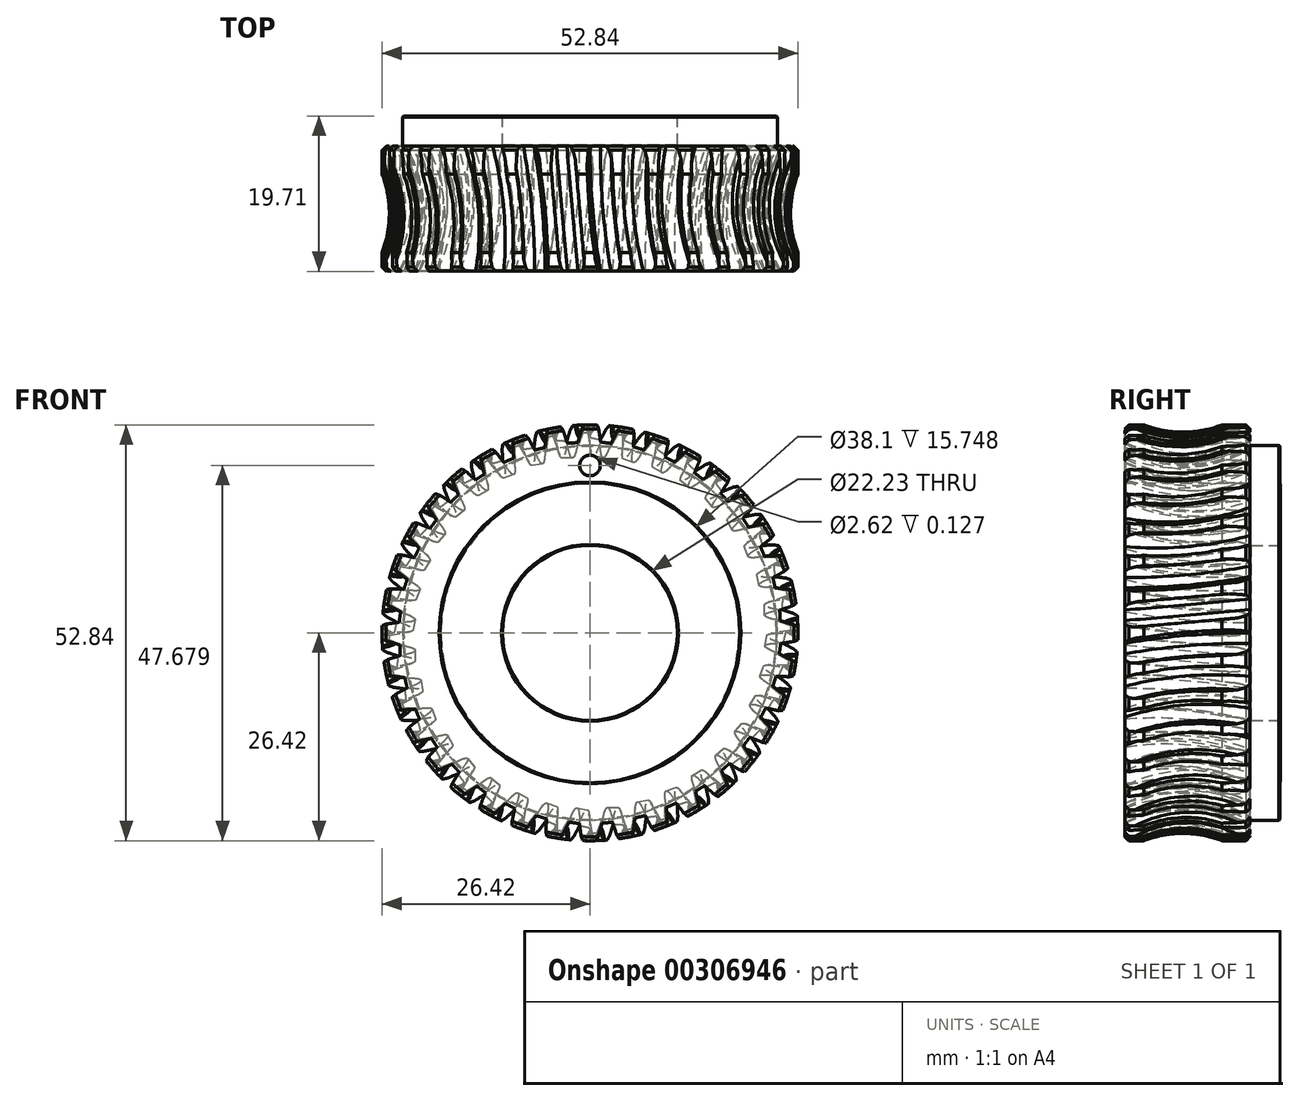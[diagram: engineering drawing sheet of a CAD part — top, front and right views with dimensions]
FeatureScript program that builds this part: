
annotation { "Feature Type Name" : "Feature", "Feature Type Description" : "" }
export const myFeature = defineFeature(function(context is Context, id is Id, definition is map)
    precondition{}
    {
        {
            var Q0;
            Q0=qCreatedBy(makeId("Front.planeOp"),FACE);
            var sketch = newSketch(context, id + "F0", { "sketchPlane" : qUnion([Q0])});
            skCircle(sketch, "E0", {"center": v(0, 0) * mm, "radius": 26.42 * mm});
            skCircle(sketch, "E1", {"center": v(0, 0) * mm, "radius": 11.11 * mm});
            skCircle(sketch, "E2", {"center": v(0, 0) * mm, "radius": 19.05 * mm});
            skSolve(sketch);
        }
        {
            var Q0;
            Q0=makeQuery(id+"F0.imprint","IMPRINT",FACE,{"disambiguationData":[TD([[makeQuery(id+"F0.imprint","IMPRINT",EDGE,{"derivedFrom":sQuery(id+"F0.wireOp",EDGE,"E0")}),1.0]])]});
            extrude(context, id + "F1", {"entities" : qUnion([Q0]), "endBound" : BoundingType.SYMMETRIC, "depth" : 15.88 * mm});
        }
        {
            var Q0;
            Q0=makeQuery(id+"F1.opExtrude","CAP_EDGE",EDGE,{"disambiguationData":[OSD([sQuery(id+"F0.wireOp",EDGE,"E0")])],"isStart":true});
            var Q1;
            Q1=makeQuery(id+"F1.opExtrude","CAP_EDGE",EDGE,{"disambiguationData":[OSD([sQuery(id+"F0.wireOp",EDGE,"E0")])],"isStart":false});
            chamfer(context, id + "F2", {"entities" : qUnion([Q0, Q1]), "width" : 0.5 * mm, "tangentPropagation" : true});
        }
        {
            var Q0;
            Q0=qCreatedBy(makeId("Top.planeOp"),FACE);
            var sketch = newSketch(context, id + "F3", { "sketchPlane" : qUnion([Q0])});
            skLineSegment(sketch, "E3", {"start": v(-49.13, -51.5) * mm, "end": v(57.98, -51.5) * mm});
            skSolve(sketch);
        }
        {
            var Q0;
            Q0=sQuery(id+"F3.wireOp",EDGE,"E3");
            cPlane(context, id + "F4", {"entities" : qUnion([Q0]), "cplaneType" : CPlaneType.LINE_ANGLE, "offset" : 25.4 * mm, "angle" : 85 * degree, "oppositeDirection" : true, "width" : 152.4 * mm, "height" : 152.4 * mm});
        }
        {
            var Q0;
            Q0=qCreatedBy(id+"F4.planeOp",FACE);
            var sketch = newSketch(context, id + "F5", { "sketchPlane" : qUnion([Q0])});
            skCircle(sketch, "E4", {"center": v(38.56, 0) * mm, "radius": 16.37 * mm});
            skCircle(sketch, "E5", {"center": v(38.56, 0) * mm, "radius": 13.48 * mm});
            skSolve(sketch);
        }
        {
            var Q0;
            Q0=makeQuery(id+"F5.imprint","IMPRINT",FACE,{"disambiguationData":[TD([[makeQuery(id+"F5.imprint","IMPRINT",EDGE,{"derivedFrom":sQuery(id+"F5.wireOp",EDGE,"E4")}),1.0]])]});
            var Q1;
            Q1=makeQuery(id+"F5.imprint","IMPRINT",FACE,{"disambiguationData":[TD([[makeQuery(id+"F5.imprint","IMPRINT",EDGE,{"derivedFrom":sQuery(id+"F5.wireOp",EDGE,"E5")}),1.0]])]});
            extrude(context, id + "F6", {"entities" : qUnion([Q0, Q1]), "depth" : 3.17 * mm});
        }
        {
            var Q0;
            Q0=makeQuery(id+"F6.opExtrude","CAP_EDGE",EDGE,{"disambiguationData":[OSD([sQuery(id+"F5.wireOp",EDGE,"E4")])],"isStart":false});
            var Q1;
            Q1=makeQuery(id+"F6.opExtrude","CAP_EDGE",EDGE,{"disambiguationData":[OSD([sQuery(id+"F5.wireOp",EDGE,"E4")])],"isStart":true});
            chamfer(context, id + "F7", {"entities" : qUnion([Q0, Q1]), "chamferType" : ChamferType.OFFSET_ANGLE, "width" : 2.54 * mm, "oppositeDirection" : false, "angle" : 20 * degree, "tangentPropagation" : true});
        }
        {
            var Q0;
            Q0=makeQuery(id+"F6.opExtrude","SWEPT_BODY",BODY,{"disambiguationData":[OSD([sQuery(id+"F5.wireOp",EDGE,"E4")])]});
            var Q1;
            Q1=makeQuery(id+"F1.opExtrude","SWEPT_FACE",FACE,{"disambiguationData":[OSD([sQuery(id+"F0.wireOp",EDGE,"E2")])]});
            circularPattern(context, id + "F8", {"entities" : qUnion([Q0]), "axis" : qUnion([Q1]), "angle" : 360 * degree, "instanceCount" : 36, "equalSpace" : true});
        }
        {
            var Q0;
            Q0=makeQuery(id+"F8.opPattern","COPY",BODY,{"derivedFrom":makeQuery(id+"F6.opExtrude","SWEPT_BODY",BODY,{"disambiguationData":[OSD([sQuery(id+"F5.wireOp",EDGE,"E4")])]}),"instanceName":"25"});
            var Q1;
            Q1=makeQuery(id+"F8.opPattern","COPY",BODY,{"derivedFrom":makeQuery(id+"F6.opExtrude","SWEPT_BODY",BODY,{"disambiguationData":[OSD([sQuery(id+"F5.wireOp",EDGE,"E4")])]}),"instanceName":"24"});
            var Q2;
            Q2=makeQuery(id+"F8.opPattern","COPY",BODY,{"derivedFrom":makeQuery(id+"F6.opExtrude","SWEPT_BODY",BODY,{"disambiguationData":[OSD([sQuery(id+"F5.wireOp",EDGE,"E4")])]}),"instanceName":"23"});
            var Q3;
            Q3=makeQuery(id+"F8.opPattern","COPY",BODY,{"derivedFrom":makeQuery(id+"F6.opExtrude","SWEPT_BODY",BODY,{"disambiguationData":[OSD([sQuery(id+"F5.wireOp",EDGE,"E4")])]}),"instanceName":"22"});
            var Q4;
            Q4=makeQuery(id+"F8.opPattern","COPY",BODY,{"derivedFrom":makeQuery(id+"F6.opExtrude","SWEPT_BODY",BODY,{"disambiguationData":[OSD([sQuery(id+"F5.wireOp",EDGE,"E4")])]}),"instanceName":"21"});
            var Q5;
            Q5=makeQuery(id+"F8.opPattern","COPY",BODY,{"derivedFrom":makeQuery(id+"F6.opExtrude","SWEPT_BODY",BODY,{"disambiguationData":[OSD([sQuery(id+"F5.wireOp",EDGE,"E4")])]}),"instanceName":"20"});
            var Q6;
            Q6=makeQuery(id+"F8.opPattern","COPY",BODY,{"derivedFrom":makeQuery(id+"F6.opExtrude","SWEPT_BODY",BODY,{"disambiguationData":[OSD([sQuery(id+"F5.wireOp",EDGE,"E4")])]}),"instanceName":"19"});
            var Q7;
            Q7=makeQuery(id+"F8.opPattern","COPY",BODY,{"derivedFrom":makeQuery(id+"F6.opExtrude","SWEPT_BODY",BODY,{"disambiguationData":[OSD([sQuery(id+"F5.wireOp",EDGE,"E4")])]}),"instanceName":"18"});
            var Q8;
            Q8=makeQuery(id+"F8.opPattern","COPY",BODY,{"derivedFrom":makeQuery(id+"F6.opExtrude","SWEPT_BODY",BODY,{"disambiguationData":[OSD([sQuery(id+"F5.wireOp",EDGE,"E4")])]}),"instanceName":"17"});
            var Q9;
            Q9=makeQuery(id+"F8.opPattern","COPY",BODY,{"derivedFrom":makeQuery(id+"F6.opExtrude","SWEPT_BODY",BODY,{"disambiguationData":[OSD([sQuery(id+"F5.wireOp",EDGE,"E4")])]}),"instanceName":"16"});
            var Q10;
            Q10=makeQuery(id+"F8.opPattern","COPY",BODY,{"derivedFrom":makeQuery(id+"F6.opExtrude","SWEPT_BODY",BODY,{"disambiguationData":[OSD([sQuery(id+"F5.wireOp",EDGE,"E4")])]}),"instanceName":"15"});
            var Q11;
            Q11=makeQuery(id+"F8.opPattern","COPY",BODY,{"derivedFrom":makeQuery(id+"F6.opExtrude","SWEPT_BODY",BODY,{"disambiguationData":[OSD([sQuery(id+"F5.wireOp",EDGE,"E4")])]}),"instanceName":"14"});
            var Q12;
            Q12=makeQuery(id+"F8.opPattern","COPY",BODY,{"derivedFrom":makeQuery(id+"F6.opExtrude","SWEPT_BODY",BODY,{"disambiguationData":[OSD([sQuery(id+"F5.wireOp",EDGE,"E4")])]}),"instanceName":"13"});
            var Q13;
            Q13=makeQuery(id+"F8.opPattern","COPY",BODY,{"derivedFrom":makeQuery(id+"F6.opExtrude","SWEPT_BODY",BODY,{"disambiguationData":[OSD([sQuery(id+"F5.wireOp",EDGE,"E4")])]}),"instanceName":"12"});
            var Q14;
            Q14=makeQuery(id+"F8.opPattern","COPY",BODY,{"derivedFrom":makeQuery(id+"F6.opExtrude","SWEPT_BODY",BODY,{"disambiguationData":[OSD([sQuery(id+"F5.wireOp",EDGE,"E4")])]}),"instanceName":"11"});
            var Q15;
            Q15=makeQuery(id+"F8.opPattern","COPY",BODY,{"derivedFrom":makeQuery(id+"F6.opExtrude","SWEPT_BODY",BODY,{"disambiguationData":[OSD([sQuery(id+"F5.wireOp",EDGE,"E4")])]}),"instanceName":"10"});
            var Q16;
            Q16=makeQuery(id+"F8.opPattern","COPY",BODY,{"derivedFrom":makeQuery(id+"F6.opExtrude","SWEPT_BODY",BODY,{"disambiguationData":[OSD([sQuery(id+"F5.wireOp",EDGE,"E4")])]}),"instanceName":"9"});
            var Q17;
            Q17=makeQuery(id+"F8.opPattern","COPY",BODY,{"derivedFrom":makeQuery(id+"F6.opExtrude","SWEPT_BODY",BODY,{"disambiguationData":[OSD([sQuery(id+"F5.wireOp",EDGE,"E4")])]}),"instanceName":"8"});
            var Q18;
            Q18=makeQuery(id+"F8.opPattern","COPY",BODY,{"derivedFrom":makeQuery(id+"F6.opExtrude","SWEPT_BODY",BODY,{"disambiguationData":[OSD([sQuery(id+"F5.wireOp",EDGE,"E4")])]}),"instanceName":"7"});
            var Q19;
            Q19=makeQuery(id+"F8.opPattern","COPY",BODY,{"derivedFrom":makeQuery(id+"F6.opExtrude","SWEPT_BODY",BODY,{"disambiguationData":[OSD([sQuery(id+"F5.wireOp",EDGE,"E4")])]}),"instanceName":"6"});
            var Q20;
            Q20=makeQuery(id+"F8.opPattern","COPY",BODY,{"derivedFrom":makeQuery(id+"F6.opExtrude","SWEPT_BODY",BODY,{"disambiguationData":[OSD([sQuery(id+"F5.wireOp",EDGE,"E4")])]}),"instanceName":"5"});
            var Q21;
            Q21=makeQuery(id+"F8.opPattern","COPY",BODY,{"derivedFrom":makeQuery(id+"F6.opExtrude","SWEPT_BODY",BODY,{"disambiguationData":[OSD([sQuery(id+"F5.wireOp",EDGE,"E4")])]}),"instanceName":"4"});
            var Q22;
            Q22=makeQuery(id+"F8.opPattern","COPY",BODY,{"derivedFrom":makeQuery(id+"F6.opExtrude","SWEPT_BODY",BODY,{"disambiguationData":[OSD([sQuery(id+"F5.wireOp",EDGE,"E4")])]}),"instanceName":"3"});
            var Q23;
            Q23=makeQuery(id+"F8.opPattern","COPY",BODY,{"derivedFrom":makeQuery(id+"F6.opExtrude","SWEPT_BODY",BODY,{"disambiguationData":[OSD([sQuery(id+"F5.wireOp",EDGE,"E4")])]}),"instanceName":"2"});
            var Q24;
            Q24=makeQuery(id+"F8.opPattern","COPY",BODY,{"derivedFrom":makeQuery(id+"F6.opExtrude","SWEPT_BODY",BODY,{"disambiguationData":[OSD([sQuery(id+"F5.wireOp",EDGE,"E4")])]}),"instanceName":"1"});
            var Q25;
            Q25=makeQuery(id+"F6.opExtrude","SWEPT_BODY",BODY,{"disambiguationData":[OSD([sQuery(id+"F5.wireOp",EDGE,"E4")])]});
            var Q26;
            Q26=makeQuery(id+"F8.opPattern","COPY",BODY,{"derivedFrom":makeQuery(id+"F6.opExtrude","SWEPT_BODY",BODY,{"disambiguationData":[OSD([sQuery(id+"F5.wireOp",EDGE,"E4")])]}),"instanceName":"35"});
            var Q27;
            Q27=makeQuery(id+"F8.opPattern","COPY",BODY,{"derivedFrom":makeQuery(id+"F6.opExtrude","SWEPT_BODY",BODY,{"disambiguationData":[OSD([sQuery(id+"F5.wireOp",EDGE,"E4")])]}),"instanceName":"34"});
            var Q28;
            Q28=makeQuery(id+"F8.opPattern","COPY",BODY,{"derivedFrom":makeQuery(id+"F6.opExtrude","SWEPT_BODY",BODY,{"disambiguationData":[OSD([sQuery(id+"F5.wireOp",EDGE,"E4")])]}),"instanceName":"33"});
            var Q29;
            Q29=makeQuery(id+"F8.opPattern","COPY",BODY,{"derivedFrom":makeQuery(id+"F6.opExtrude","SWEPT_BODY",BODY,{"disambiguationData":[OSD([sQuery(id+"F5.wireOp",EDGE,"E4")])]}),"instanceName":"32"});
            var Q30;
            Q30=makeQuery(id+"F8.opPattern","COPY",BODY,{"derivedFrom":makeQuery(id+"F6.opExtrude","SWEPT_BODY",BODY,{"disambiguationData":[OSD([sQuery(id+"F5.wireOp",EDGE,"E4")])]}),"instanceName":"31"});
            var Q31;
            Q31=makeQuery(id+"F8.opPattern","COPY",BODY,{"derivedFrom":makeQuery(id+"F6.opExtrude","SWEPT_BODY",BODY,{"disambiguationData":[OSD([sQuery(id+"F5.wireOp",EDGE,"E4")])]}),"instanceName":"30"});
            var Q32;
            Q32=makeQuery(id+"F8.opPattern","COPY",BODY,{"derivedFrom":makeQuery(id+"F6.opExtrude","SWEPT_BODY",BODY,{"disambiguationData":[OSD([sQuery(id+"F5.wireOp",EDGE,"E4")])]}),"instanceName":"29"});
            var Q33;
            Q33=makeQuery(id+"F8.opPattern","COPY",BODY,{"derivedFrom":makeQuery(id+"F6.opExtrude","SWEPT_BODY",BODY,{"disambiguationData":[OSD([sQuery(id+"F5.wireOp",EDGE,"E4")])]}),"instanceName":"28"});
            var Q34;
            Q34=makeQuery(id+"F8.opPattern","COPY",BODY,{"derivedFrom":makeQuery(id+"F6.opExtrude","SWEPT_BODY",BODY,{"disambiguationData":[OSD([sQuery(id+"F5.wireOp",EDGE,"E4")])]}),"instanceName":"27"});
            var Q35;
            Q35=makeQuery(id+"F8.opPattern","COPY",BODY,{"derivedFrom":makeQuery(id+"F6.opExtrude","SWEPT_BODY",BODY,{"disambiguationData":[OSD([sQuery(id+"F5.wireOp",EDGE,"E4")])]}),"instanceName":"26"});
            var Q36;
            Q36=makeQuery(id+"F1.opExtrude","SWEPT_BODY",BODY,{"disambiguationData":[OSD([sQuery(id+"F0.wireOp",EDGE,"E0"),sQuery(id+"F0.wireOp",EDGE,"E2")])]});
            booleanBodies(context, id + "F9", {"operationType" : BooleanOperationType.SUBTRACTION, "tools" : qUnion([Q0, Q1, Q2, Q3, Q4, Q5, Q6, Q7, Q8, Q9, Q10, Q11, Q12, Q13, Q14, Q15, Q16, Q17, Q18, Q19, Q20, Q21, Q22, Q23, Q24, Q25, Q26, Q27, Q28, Q29, Q30, Q31, Q32, Q33, Q34, Q35]), "targets" : qUnion([Q36])});
        }
        {
            var Q0;
            Q0=makeQuery(id+"F5.imprint","IMPRINT",FACE,{"disambiguationData":[TD([[makeQuery(id+"F5.imprint","IMPRINT",EDGE,{"derivedFrom":sQuery(id+"F5.wireOp",EDGE,"E5")}),1.0]])]});
            var Q1;
            Q1=makeQuery(id+"F1.opExtrude","SWEPT_FACE",FACE,{"disambiguationData":[OSD([sQuery(id+"F0.wireOp",EDGE,"E2")])]});
            revolve(context, id + "F10", {"operationType" : NewBodyOperationType.REMOVE, "entities" : qUnion([Q0]), "axis" : qUnion([Q1]), "revolveType" : RevolveType.FULL, "oppositeDirection" : true});
        }
        {
            var Q0;
            Q0=makeQuery(id+"F1.opExtrude","CAP_FACE",FACE,{"disambiguationData":[OSD([sQuery(id+"F0.wireOp",EDGE,"E0"),sQuery(id+"F0.wireOp",EDGE,"E2")])],"isStart":true});
            var sketch = newSketch(context, id + "F11", { "sketchPlane" : qUnion([Q0])});
            skCircle(sketch, "E6", {"center": v(0, 0) * mm, "radius": 23.81 * mm});
            skSolve(sketch);
        }
        {
            var Q0;
            {var subQ2=sQuery(id+"F0.wireOp",EDGE,"E2");Q0=makeQuery(id+"F11.imprint","IMPRINT",FACE,{"disambiguationData":[TD([[makeQuery(id+"F11.imprint","IMPRINT",EDGE,{"derivedFrom":makeQuery(id+"F1.opExtrude","CAP_EDGE",EDGE,{"disambiguationData":[OSD([subQ2])],"isStart":true})}),1.0]])]});}
            extrude(context, id + "F12", {"entities" : qUnion([Q0]), "operationType" : NewBodyOperationType.ADD, "depth" : 3.8 * mm});
        }
        {
            var Q0;
            Q0=makeQuery(id+"F12.opExtrude","CAP_FACE",FACE,{"disambiguationData":[OSD([sQuery(id+"F0.wireOp",EDGE,"E0"),sQuery(id+"F0.wireOp",EDGE,"E2"),sQuery(id+"FC3Jd3sHyPeDAeg_1.wireOp",EDGE,"79b9966f-34db-4600-b145-85a5b1c19bfb"),sQuery(id+"F11.wireOp",EDGE,"E6")])],"isStart":false});
            var sketch = newSketch(context, id + "F13", { "sketchPlane" : qUnion([Q0])});
            skCircle(sketch, "E7", {"center": v(0, 0) * mm, "radius": 19.05 * mm});
            skSolve(sketch);
        }
        {
            var Q0;
            Q0=makeQuery(id+"F13.imprint","IMPRINT",FACE,{"disambiguationData":[TD([[makeQuery(id+"F13.imprint","IMPRINT",EDGE,{"derivedFrom":sQuery(id+"F13.wireOp",EDGE,"E7")}),-1.0]])]});
            extrude(context, id + "F14", {"entities" : qUnion([Q0]), "operationType" : NewBodyOperationType.ADD, "depth" : 9 / 406.4 * mm, "hasSecondDirection" : true, "secondDirectionOppositeDirection" : true, "secondDirectionDepth" : 3.8 * mm});
        }
        {
            var Q0;
            Q0=makeQuery(id+"F14.opExtrude","CAP_FACE",FACE,{"disambiguationData":[OSD([sQuery(id+"F13.wireOp",EDGE,"E7")])],"isStart":false});
            var sketch = newSketch(context, id + "F15", { "sketchPlane" : qUnion([Q0])});
            skCircle(sketch, "E8", {"center": v(0, 0) * mm, "radius": 11.11 * mm});
            skSolve(sketch);
        }
        {
            var Q0;
            Q0=makeQuery(id+"F15.imprint","IMPRINT",FACE,{"disambiguationData":[TD([[makeQuery(id+"F15.imprint","IMPRINT",EDGE,{"derivedFrom":sQuery(id+"F15.wireOp",EDGE,"E8")}),1.0]])]});
            extrude(context, id + "F16", {"entities" : qUnion([Q0]), "operationType" : NewBodyOperationType.REMOVE, "endBound" : BoundingType.THROUGH_ALL, "oppositeDirection" : true, "depth" : 25.4 * mm});
        }
        {
            var Q0;
            Q0=qCreatedBy(makeId("Right.planeOp"),FACE);
            var sketch = newSketch(context, id + "F17", { "sketchPlane" : qUnion([Q0])});
            skLineSegment(sketch, "E9.bottom", {"start": v(15.58, 19.07) * mm, "end": v(11.77, 19.07) * mm});
            skLineSegment(sketch, "E9.top", {"start": v(15.58, 18.75) * mm, "end": v(11.77, 18.75) * mm});
            skLineSegment(sketch, "E9.left", {"start": v(15.58, 19.07) * mm, "end": v(15.58, 18.75) * mm});
            skLineSegment(sketch, "E9.right", {"start": v(11.77, 19.07) * mm, "end": v(11.77, 18.75) * mm});
            skSolve(sketch);
        }
        {
            var Q0;
            Q0=makeQuery(id+"F17.imprint","IMPRINT",FACE,{"disambiguationData":[TD([[makeQuery(id+"F17.imprint","IMPRINT",EDGE,{"derivedFrom":sQuery(id+"F17.wireOp",EDGE,"E9.bottom")}),1.0]])]});
            var Q1;
            Q1=makeQuery(id+"F16.boolean.opBoolean","COPY",FACE,{"derivedFrom":makeQuery(id+"F16.opExtrude","SWEPT_FACE",FACE,{"disambiguationData":[OSD([sQuery(id+"F15.wireOp",EDGE,"E8")])]})});
            revolve(context, id + "F18", {"operationType" : NewBodyOperationType.REMOVE, "entities" : qUnion([Q0]), "axis" : qUnion([Q1]), "revolveType" : RevolveType.FULL, "oppositeDirection" : true});
        }
        {
            var Q0;
            Q0=makeQuery(id+"F14.opExtrude","CAP_EDGE",EDGE,{"disambiguationData":[OSD([sQuery(id+"F13.wireOp",EDGE,"E7")])],"isStart":false});
            var Q1;
            Q1=makeQuery(id+"F16.boolean.opBoolean","COPY",EDGE,{"derivedFrom":makeQuery(id+"F16.opExtrude","CAP_EDGE",EDGE,{"disambiguationData":[OSD([sQuery(id+"F15.wireOp",EDGE,"E8")])],"isStart":true})});
            var Q2;
            Q2=makeQuery(id+"F1.opExtrude","CAP_EDGE",EDGE,{"disambiguationData":[OSD([sQuery(id+"F0.wireOp",EDGE,"E2")])],"isStart":false});
            var Q3;
            Q3=makeQuery(id+"F14.opExtrude","CAP_EDGE",EDGE,{"disambiguationData":[OSD([sQuery(id+"F13.wireOp",EDGE,"E7")])],"isStart":true});
            var Q4;
            Q4=makeQuery(id+"F16.boolean.opBoolean","INTERSECT",EDGE,{"derivedFrom":[makeQuery(id+"F14.opExtrude","CAP_FACE",FACE,{"disambiguationData":[OSD([sQuery(id+"F13.wireOp",EDGE,"E7")])],"isStart":true}),makeQuery(id+"F16.opExtrude","SWEPT_FACE",FACE,{"disambiguationData":[OSD([sQuery(id+"F15.wireOp",EDGE,"E8")])]})]});
            var Q5;
            Q5=makeQuery(id+"F12.opExtrude","CAP_EDGE",EDGE,{"disambiguationData":[OSD([sQuery(id+"F11.wireOp",EDGE,"E6")])],"isStart":false});
            var Q6;
            Q6=makeQuery(id+"F18.boolean.opBoolean","COPY",EDGE,{"derivedFrom":makeQuery(id+"F18.opRevolve","SWEPT_EDGE",EDGE,{"disambiguationData":[OSD([sQuery(id+"F17.wireOp",EDGE,"E9.top"),sQuery(id+"F17.wireOp",EDGE,"E9.right")])]})});
            var Q7;
            Q7=makeQuery(id+"F18.boolean.opBoolean","COPY",EDGE,{"derivedFrom":makeQuery(id+"F18.opRevolve","SWEPT_EDGE",EDGE,{"disambiguationData":[OSD([sQuery(id+"F17.wireOp",EDGE,"E9.top"),sQuery(id+"F17.wireOp",EDGE,"E9.left")])]})});
            var Q8;
            Q8=makeQuery(id+"F18.boolean.opBoolean","INTERSECT",EDGE,{"derivedFrom":[makeQuery(id+"F14.opExtrude","SWEPT_FACE",FACE,{"disambiguationData":[OSD([sQuery(id+"F13.wireOp",EDGE,"E7")])]}),makeQuery(id+"F18.opRevolve","SWEPT_FACE",FACE,{"disambiguationData":[OSD([sQuery(id+"F17.wireOp",EDGE,"E9.left")])]})]});
            chamfer(context, id + "F19", {"entities" : qUnion([Q0, Q1, Q2, Q3, Q4, Q5, Q6, Q7, Q8]), "width" : 0.13 * mm, "tangentPropagation" : true});
        }
        {
            var Q0;
            Q0=makeQuery(id+"F1.opExtrude","CAP_FACE",FACE,{"disambiguationData":[OSD([sQuery(id+"F0.wireOp",EDGE,"E0"),sQuery(id+"F0.wireOp",EDGE,"E2")])],"isStart":false});
            var sketch = newSketch(context, id + "F20", { "sketchPlane" : qUnion([Q0])});
            skCircle(sketch, "E10", {"center": v(0, 21.26) * mm, "radius": 1.3 * mm});
            skSolve(sketch);
        }
        {
            var Q0;
            Q0=makeQuery(id+"F20.imprint","IMPRINT",FACE,{"disambiguationData":[TD([[makeQuery(id+"F20.imprint","IMPRINT",EDGE,{"derivedFrom":sQuery(id+"F20.wireOp",EDGE,"E10")}),1.0]])]});
            extrude(context, id + "F21", {"entities" : qUnion([Q0]), "operationType" : NewBodyOperationType.REMOVE, "oppositeDirection" : true, "depth" : 0.13 * mm});
        }
    });
